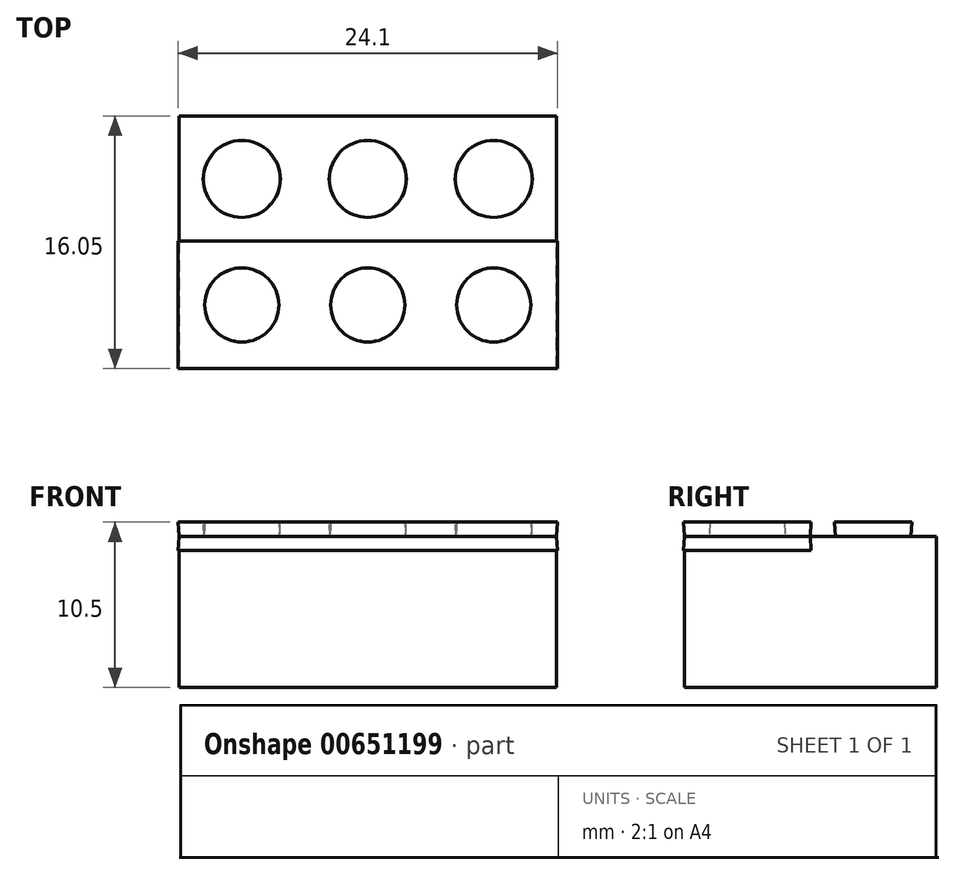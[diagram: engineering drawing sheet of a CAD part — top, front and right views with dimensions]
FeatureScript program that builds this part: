
annotation { "Feature Type Name" : "Feature", "Feature Type Description" : "" }
export const myFeature = defineFeature(function(context is Context, id is Id, definition is map)
    precondition{}
    {
        {
            var Q0;
            Q0=qCreatedBy(makeId("Top.planeOp"),FACE);
            var sketch = newSketch(context, id + "F0", { "sketchPlane" : qUnion([Q0])});
            skLineSegment(sketch, "E0.bottom", {"start": v(0, 0) * mm, "end": v(-24, 0) * mm});
            skLineSegment(sketch, "E0.top", {"start": v(0, 16) * mm, "end": v(-24, 16) * mm});
            skLineSegment(sketch, "E0.left", {"start": v(0, 0) * mm, "end": v(0, 16) * mm});
            skLineSegment(sketch, "E0.right", {"start": v(-24, 0) * mm, "end": v(-24, 16) * mm});
            skSolve(sketch);
        }
        {
            var Q0;
            Q0=makeQuery(id+"F0.imprint","IMPRINT",FACE,{"disambiguationData":[TD([[makeQuery(id+"F0.imprint","IMPRINT",EDGE,{"derivedFrom":sQuery(id+"F0.wireOp",EDGE,"E0.bottom")}),-1.0]])]});
            extrude(context, id + "F1", {"entities" : qUnion([Q0]), "depth" : 9.6 * mm, "offsetDistance" : 25.4 * mm});
        }
        {
            var Q0;
            Q0=makeQuery(id+"F1.opExtrude","CAP_FACE",FACE,{"disambiguationData":[OSD([sQuery(id+"F0.wireOp",EDGE,"E0.bottom"),sQuery(id+"F0.wireOp",EDGE,"E0.top"),sQuery(id+"F0.wireOp",EDGE,"E0.left"),sQuery(id+"F0.wireOp",EDGE,"E0.right")])],"isStart":false});
            var sketch = newSketch(context, id + "F2", { "sketchPlane" : qUnion([Q0])});
            skLineSegment(sketch, "E1", {"start": v(-24, 8) * mm, "end": v(0, 8) * mm});
            skLineSegment(sketch, "E2", {"start": v(-16, 16) * mm, "end": v(-16, 0) * mm});
            skLineSegment(sketch, "E3", {"start": v(-8, 16) * mm, "end": v(-8, 0) * mm});
            skLineSegment(sketch, "E4", {"start": v(-24, 16) * mm, "end": v(-16, 8) * mm});
            skLineSegment(sketch, "E5", {"start": v(-16, 8) * mm, "end": v(-8, 16) * mm});
            skLineSegment(sketch, "E6", {"start": v(-8, 16) * mm, "end": v(0, 8) * mm});
            skCircle(sketch, "E7", {"center": v(-20, 12) * mm, "radius": 2.4 * mm});
            skCircle(sketch, "E8", {"center": v(-12, 12) * mm, "radius": 2.4 * mm});
            skCircle(sketch, "E9", {"center": v(-4, 12) * mm, "radius": 2.4 * mm});
            skCircle(sketch, "E10.MirrorC", {"center": v(-20, 4) * mm, "radius": 2.4 * mm});
            skCircle(sketch, "E11.MirrorC", {"center": v(-12, 4) * mm, "radius": 2.4 * mm});
            skCircle(sketch, "E12.MirrorC", {"center": v(-4, 4) * mm, "radius": 2.4 * mm});
            skSolve(sketch);
        }
        {
            var Q0;
            Q0=makeQuery(id+"F2.imprint","IMPRINT",FACE,{"disambiguationData":[TD([[makeQuery(id+"F2.imprint","IMPRINT",EDGE,{"derivedFrom":sQuery(id+"F2.wireOp",EDGE,"E10.MirrorC")}),-1.0]])]});
            var Q1;
            Q1=makeQuery(id+"F2.imprint","IMPRINT",FACE,{"disambiguationData":[TD([[makeQuery(id+"F2.imprint","IMPRINT",EDGE,{"derivedFrom":sQuery(id+"F2.wireOp",EDGE,"E11.MirrorC")}),-1.0]])]});
            var Q2;
            Q2=makeQuery(id+"F2.imprint","IMPRINT",FACE,{"disambiguationData":[TD([[makeQuery(id+"F2.imprint","IMPRINT",EDGE,{"derivedFrom":sQuery(id+"F2.wireOp",EDGE,"E12.MirrorC")}),-1.0]])]});
            var Q3;
            {var subQ0=sQuery(id+"F2.wireOp",EDGE,"E9");var subQ1=sQuery(id+"F2.wireOp",EDGE,"E6");var subQ2=makeQuery(id+"F2.imprint","INTERSECT",VERTEX,{"disambiguationData":[OD(0.0)],"derivedFrom":[subQ1,subQ0]});Q3=makeQuery(id+"F2.imprint","IMPRINT",FACE,{"disambiguationData":[TD([[makeQuery(id+"F2.imprint","IMPRINT",EDGE,{"disambiguationData":[TD([[subQ2,-1.0]])],"derivedFrom":subQ1}),-1.0]])]});}
            var Q4;
            {var subQ0=sQuery(id+"F2.wireOp",EDGE,"E9");var subQ1=sQuery(id+"F2.wireOp",EDGE,"E6");var subQ2=makeQuery(id+"F2.imprint","INTERSECT",VERTEX,{"disambiguationData":[OD(0.0)],"derivedFrom":[subQ1,subQ0]});Q4=makeQuery(id+"F2.imprint","IMPRINT",FACE,{"disambiguationData":[TD([[makeQuery(id+"F2.imprint","IMPRINT",EDGE,{"disambiguationData":[TD([[subQ2,-1.0]])],"derivedFrom":subQ1}),1.0]])]});}
            var Q5;
            {var subQ0=sQuery(id+"F2.wireOp",EDGE,"E7");var subQ1=sQuery(id+"F2.wireOp",EDGE,"E4");var subQ2=makeQuery(id+"F2.imprint","INTERSECT",VERTEX,{"disambiguationData":[OD(0.0)],"derivedFrom":[subQ1,subQ0]});Q5=makeQuery(id+"F2.imprint","IMPRINT",FACE,{"disambiguationData":[TD([[makeQuery(id+"F2.imprint","IMPRINT",EDGE,{"disambiguationData":[TD([[subQ2,-1.0]])],"derivedFrom":subQ1}),1.0]])]});}
            var Q6;
            {var subQ0=sQuery(id+"F2.wireOp",EDGE,"E7");var subQ1=sQuery(id+"F2.wireOp",EDGE,"E4");var subQ2=makeQuery(id+"F2.imprint","INTERSECT",VERTEX,{"disambiguationData":[OD(0.0)],"derivedFrom":[subQ1,subQ0]});Q6=makeQuery(id+"F2.imprint","IMPRINT",FACE,{"disambiguationData":[TD([[makeQuery(id+"F2.imprint","IMPRINT",EDGE,{"disambiguationData":[TD([[subQ2,-1.0]])],"derivedFrom":subQ1}),-1.0]])]});}
            var Q7;
            {var subQ0=sQuery(id+"F2.wireOp",EDGE,"E8");var subQ1=sQuery(id+"F2.wireOp",EDGE,"E5");var subQ2=makeQuery(id+"F2.imprint","INTERSECT",VERTEX,{"disambiguationData":[OD(0.0)],"derivedFrom":[subQ1,subQ0]});Q7=makeQuery(id+"F2.imprint","IMPRINT",FACE,{"disambiguationData":[TD([[makeQuery(id+"F2.imprint","IMPRINT",EDGE,{"disambiguationData":[TD([[subQ2,-1.0]])],"derivedFrom":subQ1}),-1.0]])]});}
            var Q8;
            {var subQ0=sQuery(id+"F2.wireOp",EDGE,"E8");var subQ1=sQuery(id+"F2.wireOp",EDGE,"E5");var subQ2=makeQuery(id+"F2.imprint","INTERSECT",VERTEX,{"disambiguationData":[OD(0.0)],"derivedFrom":[subQ1,subQ0]});Q8=makeQuery(id+"F2.imprint","IMPRINT",FACE,{"disambiguationData":[TD([[makeQuery(id+"F2.imprint","IMPRINT",EDGE,{"disambiguationData":[TD([[subQ2,-1.0]])],"derivedFrom":subQ1}),1.0]])]});}
            extrude(context, id + "F3", {"entities" : qUnion([Q0, Q1, Q2, Q3, Q4, Q5, Q6, Q7, Q8]), "operationType" : NewBodyOperationType.ADD, "endBound" : BoundingType.SYMMETRIC, "oppositeDirection" : true, "depth" : 1.8 * mm, "offsetDistance" : 25.4 * mm, "hasDraft" : true, "draftAngle" : 3 * degree});
        }
    });
